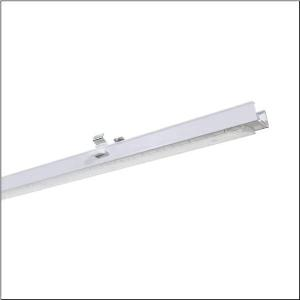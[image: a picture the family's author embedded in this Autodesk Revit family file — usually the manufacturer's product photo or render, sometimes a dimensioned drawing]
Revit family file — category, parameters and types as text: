
# Revit family: trunking_flex_31_51re18mb4cb
name_source: partatom
category: Lighting Fixtures
units: mm (PartAtom-declared; Revit-internal decimal feet)

## family parameters
Cut with Voids When Loaded = No
Host = Face
Light Source = No
Part Type = Normal
Room Calculation Point = No
Round Connector Dimension = Use Diameter
Shared = No

## types (1)
- --- (1 x LED, 11500 lm, 66 W, 4000K)
    Apparent Load = 66 VA
    CIE Flux Codes = 71 89 97 97 100
    Color Rendering = 80
    Color Temperature = 4000K
    Default Elevation = 1800 mm
    Description = Trunking Flex 31, luminaire insert, of extruded aluminium section, coated, traffic white (RAL 9016), length: 1.472mm, width: 91mm, height: 53mm, LED rated luminous flux: 11.500lm, light colour: 840, control gear: ON/OFF Multilumen, with system connector: socket, mains connection: 220..240V, AC, 50/60Hz, rated input power: 66W, connected load according to luminous flux setting (19/24/32/37/47/52/60/66W), luminous flux adjustable on luminaire in eight steps (3450/4380/5800/6700/8350/9200/10500/11500lm ), primary light control with lens, of plastic, primary optical cover: cover, of PMMA, light emission: direct distribution, protection rating (complete): IP20, insulation class (complete): insulation class I (protective earthing), certification: CE, UKCA, impact resistance: IK02, permissible ambient temperature for indoor applications: -20..+40°C, packaging unit: 1 piece
    Height = 58 mm
    Lamp = 1 x LED
    Lamp Light Flux = 11500 lm
    Lamp Power = 66 W
    Lamp count = 1
    Length = 1472 mm
    Luminous efficacy = 174 lm/W
    Manufacturer = Siteco
    ModVariant = No
    Model = 51RE18MB4CB
    Mounting Place = Ceiling
    Mounting Type = Pendant
    Number of Poles = 1
    OnlyDefault = Yes
    Power Factor = 1
    Product Name = Trunking Flex 31
    Product group = luminaire insert
    ProductGroupID = 901
    Protection Class = Protection class I
    Protection Degree = IP 20
    RLX_Detail_Level = 1
    RLX_Emergency_Light_Flux = 0 lm
    RLX_Emergency_Type = 0
    RLX_Emergency_Type_DB = No
    RlxData = <blob elided: 21177 chars, md5=bcef27f8>
    Socket = socket
    Standby Power = 0 W
    System Light Flux = 11500 lm
    System Power = 66 W
    Type Comments = factory setting: luminous flux: 100 % | (ON | ON | ON)
    Type Image = l_1266702.jpg
    URL = http://relux.com
    VarID = @adj_001177
    Voltage = 0 V
    Weight = 0.00 kg
    Width = 65 mm

## geometry (parser evidence)
native form markers: Blend x4, Sweep x11
no freeform markers — native parametric forms only
